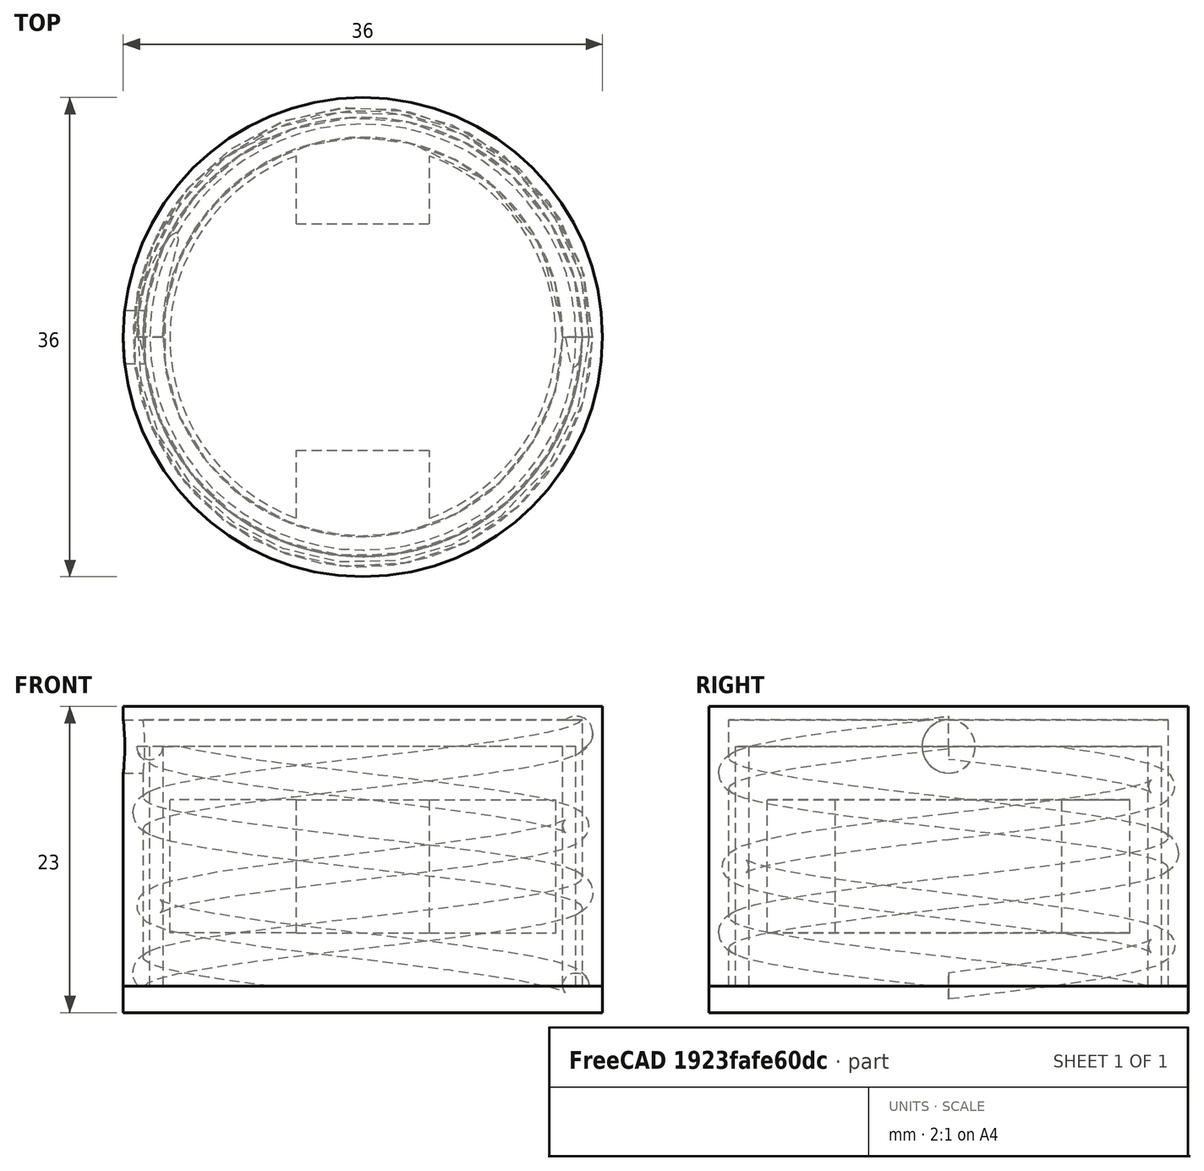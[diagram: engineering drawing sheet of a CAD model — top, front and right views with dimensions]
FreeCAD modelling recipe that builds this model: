
FCSTD DOCUMENT  (FreeCAD 0.18R16131 (Git))
Label: ws2812_bauble_ring
License: All rights reserved
LicenseURL: http://en.wikipedia.org/wiki/All_rights_reserved
objects: Part::Cylinder×7, Part::Cut×6, Part::Box×3, Part::Helix×2, PartDesign::FeatureBase×2, Sketcher::SketchObject×2, PartDesign::Body×2, Part::Sweep×2, Part::MultiFuse×1
note: 27 computed .brp shape members not serialized (recipe doc carries the construction recipe); baked Part::Feature solids carry a one-line shape summary decoded from their .brp

FEATURE [Part::Cylinder] Cylinder  label="Cylinder(ws2812_ring)"
  Angle = 360
  AttacherType = Attacher::AttachEngine3D
  Height = 10
  Radius = 14.5
FEATURE [Part::Box] Box  label="Cube(wire_cutter_top)"
  AttacherType = Attacher::AttachEngine3D
  Height = 10
  Length = 10
  Placement = pos=(-5,8.5,0) rot=(0,0,1;0rad)
  Width = 6
FEATURE [Part::Box] Box001  label="Cube001(wire_cutter_bottom)"
  AttacherType = Attacher::AttachEngine3D
  Height = 10
  Length = 10
  Placement = pos=(-5,-14.5,0) rot=(0,0,1;0rad)
  Width = 6
FEATURE [Part::Cut] Cut
  Base = -> Cylinder
  Tool = -> Box
FEATURE [Part::Cut] Cut001  label="Cut001(inner_ring_spacer)"
  Base = -> Cut
  Placement = pos=(0,0,4) rot=(0,0,1;0rad)
  Tool = -> Box001
FEATURE [Part::Cylinder] Cylinder001  label="Cylinder"
  Angle = 360
  AttacherType = Attacher::AttachEngine3D
  Height = 18
  Radius = 15
FEATURE [Part::Cylinder] Cylinder002  label="Cylinder001"
  Angle = 360
  AttacherType = Attacher::AttachEngine3D
  Height = 18
  Radius = 16
FEATURE [Part::Cut] Cut002  label="Cut002(bottle_thread_body)"
  Base = -> Cylinder002
  Tool = -> Cylinder001
FEATURE [Part::Helix] Helix
  Angle = 0
  AttacherType = Attacher::AttachEngine3D
  Height = 18
  LocalCoord = 0
  Pitch = 12
  Radius = 16
  Style = 1
FEATURE [PartDesign::FeatureBase] BaseFeature
  BaseFeature = -> Helix
FEATURE [Sketcher::SketchObject] Sketch
  ExternalGeometry = -> [BaseFeature]
  MapMode = 5
  Placement = pos=(0,0,0) rot=(1,0,0;1.5708rad)
  Support = -> [XZ_Plane]
  sketch-geometry (1):
    g0: Circle CenterX=-16 CenterY=18 CenterZ=0 NormalX=0 NormalY=0 NormalZ=1 AngleXU=0 Radius=0.98423
  constraints (1):
    c: Coincident(g0,g-3)
FEATURE [PartDesign::Body] Body  label="Body(bottle_thread)"
  BaseFeature = -> Helix
  Group = -> [BaseFeature,Sketch]
  Origin = -> Origin
  Tip = -> BaseFeature
FEATURE [Part::Sweep] Sweep  label="Sweep(bottle_thread)"
  Frenet = true
  Sections = -> [Sketch]
  Solid = true
  Spine = -> BaseFeature [Edge2,Edge1]
  Transition = 1
FEATURE [Part::Box] Box002  label="Cube"
  AttacherType = Attacher::AttachEngine3D
  Height = 10
  Length = 50
  Placement = pos=(-25,-25,18) rot=(0,0,1;0rad)
  Width = 50
FEATURE [Part::Cut] Cut003  label="Cut003(bottle_thread)"
  Base = -> Sweep
  Tool = -> Box002
FEATURE [Part::Cylinder] Cylinder003  label="Cylinder002(lid_inner)"
  Angle = 360
  AttacherType = Attacher::AttachEngine3D
  Height = 20
  Radius = 16.5
FEATURE [Part::Cylinder] Cylinder004  label="Cylinder002(lid_outer)"
  Angle = 360
  AttacherType = Attacher::AttachEngine3D
  Height = 21
  Radius = 18
FEATURE [Part::Helix] Helix001
  Angle = 0
  AttacherType = Attacher::AttachEngine3D
  Height = 24
  LocalCoord = 0
  Pitch = 12
  Radius = 16
  Style = 1
FEATURE [PartDesign::FeatureBase] BaseFeature001
  BaseFeature = -> Helix001
FEATURE [Sketcher::SketchObject] Sketch001
  ExternalGeometry = -> [BaseFeature001]
  MapMode = 5
  Placement = pos=(0,0,0) rot=(1,0,0;1.5708rad)
  Support = -> [XZ_Plane001]
  sketch-geometry (1):
    g0: Circle CenterX=16 CenterY=24 CenterZ=0 NormalX=0 NormalY=0 NormalZ=1 AngleXU=0 Radius=1.26737
  constraints (1):
    c: Coincident(g0,g-3)
FEATURE [PartDesign::Body] Body001  label="Body001(lid_thread)"
  BaseFeature = -> Helix001
  Group = -> [BaseFeature001,Sketch001]
  Origin = -> Origin001
  Tip = -> BaseFeature001
FEATURE [Part::Sweep] Sweep001  label="Sweep001(lid_thread)"
  Frenet = true
  Placement = pos=(0,0,-5) rot=(0,0,1;0rad)
  Sections = -> [Sketch001]
  Solid = true
  Spine = -> BaseFeature001 [Edge2,Edge1]
  Transition = 1
FEATURE [Part::MultiFuse] Fusion
  Shapes = -> [Cylinder003,Sweep001]
FEATURE [Part::Cut] Cut004  label="Cut004(lid)"
  Base = -> Cylinder004
  Tool = -> Fusion
FEATURE [Part::Cylinder] Cylinder005  label="Cylinder002(base)"
  Angle = 360
  AttacherType = Attacher::AttachEngine3D
  Height = 2
  Placement = pos=(0,0,-2) rot=(0,0,1;0rad)
  Radius = 18
FEATURE [Part::Cylinder] Cylinder006  label="Cylinder002(wire_hole)"
  Angle = 360
  AttacherType = Attacher::AttachEngine3D
  Height = 10
  Placement = pos=(-20,0,18) rot=(0,1,0;1.5708rad)
  Radius = 2
FEATURE [Part::Cut] Cut005  label="Cut005(lid)"
  Base = -> Cut004
  Tool = -> Cylinder006
